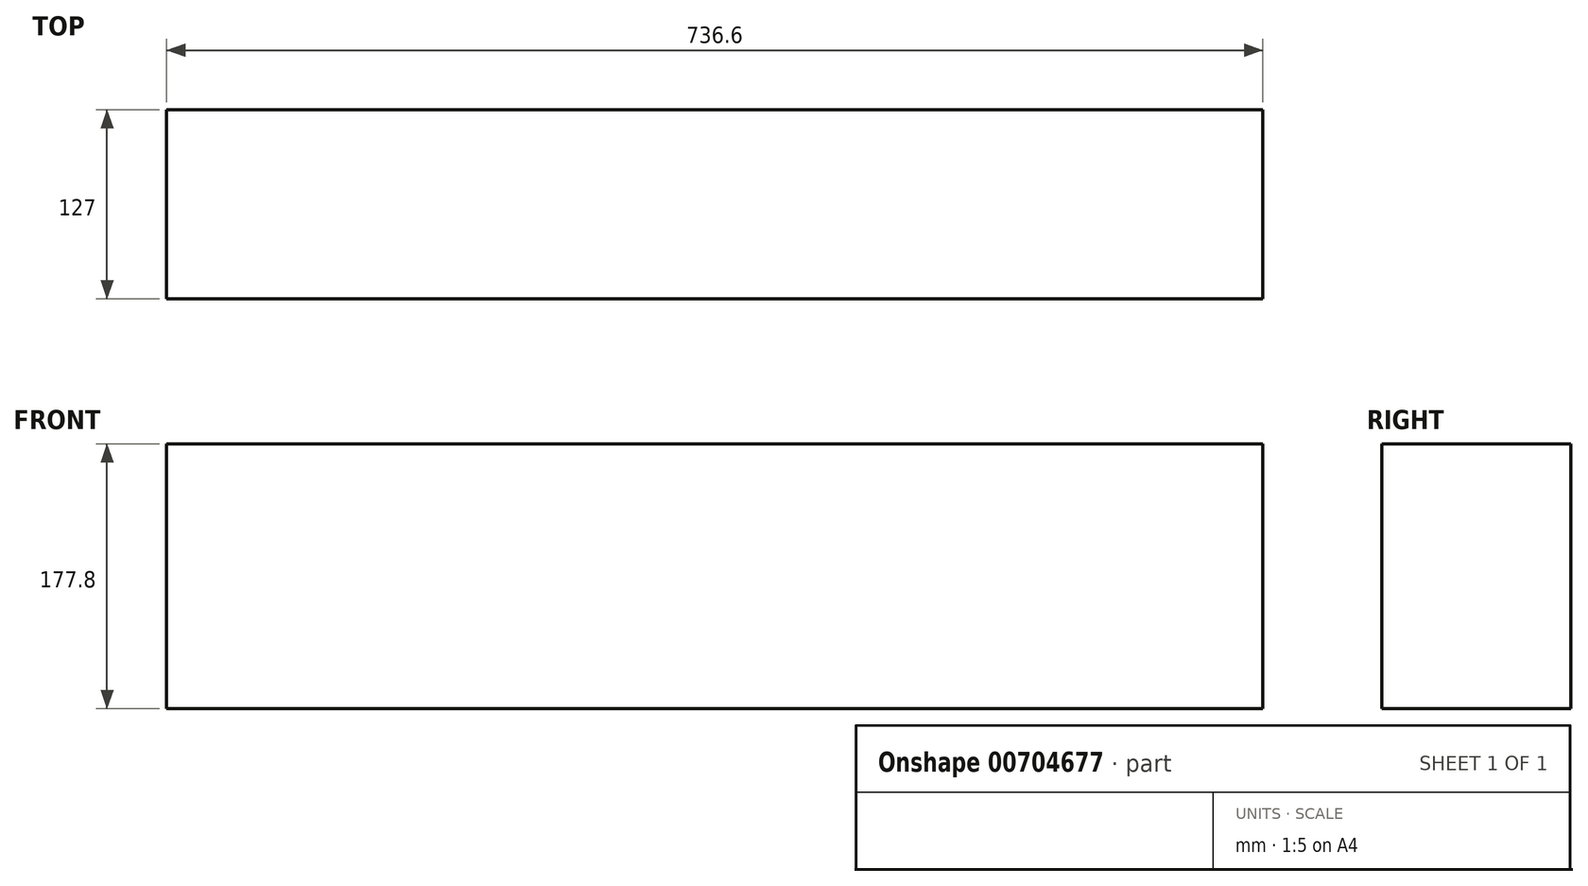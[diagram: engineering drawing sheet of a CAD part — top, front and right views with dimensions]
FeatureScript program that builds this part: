
annotation { "Feature Type Name" : "Feature", "Feature Type Description" : "" }
export const myFeature = defineFeature(function(context is Context, id is Id, definition is map)
    precondition{}
    {
        {
            var Q0;
            Q0=qCreatedBy(makeId("Top.planeOp"),FACE);
            var sketch = newSketch(context, id + "F0", { "sketchPlane" : qUnion([Q0])});
            skLineSegment(sketch, "E0.bottom", {"start": v(213.59, 127) * mm, "end": v(-523.01, 127) * mm});
            skLineSegment(sketch, "E0.top", {"start": v(213.59, 0) * mm, "end": v(-523.01, 0) * mm});
            skLineSegment(sketch, "E0.left", {"start": v(213.59, 127) * mm, "end": v(213.59, 0) * mm});
            skLineSegment(sketch, "E0.right", {"start": v(-523.01, 127) * mm, "end": v(-523.01, 0) * mm});
            skSolve(sketch);
        }
        {
            var Q0;
            Q0 = qSketchRegion(id + "F0", true);
            extrude(context, id + "F1", {"entities" : qUnion([Q0]), "depth" : 177.8 * mm, "offsetDistance" : 25.4 * mm});
        }
    });
